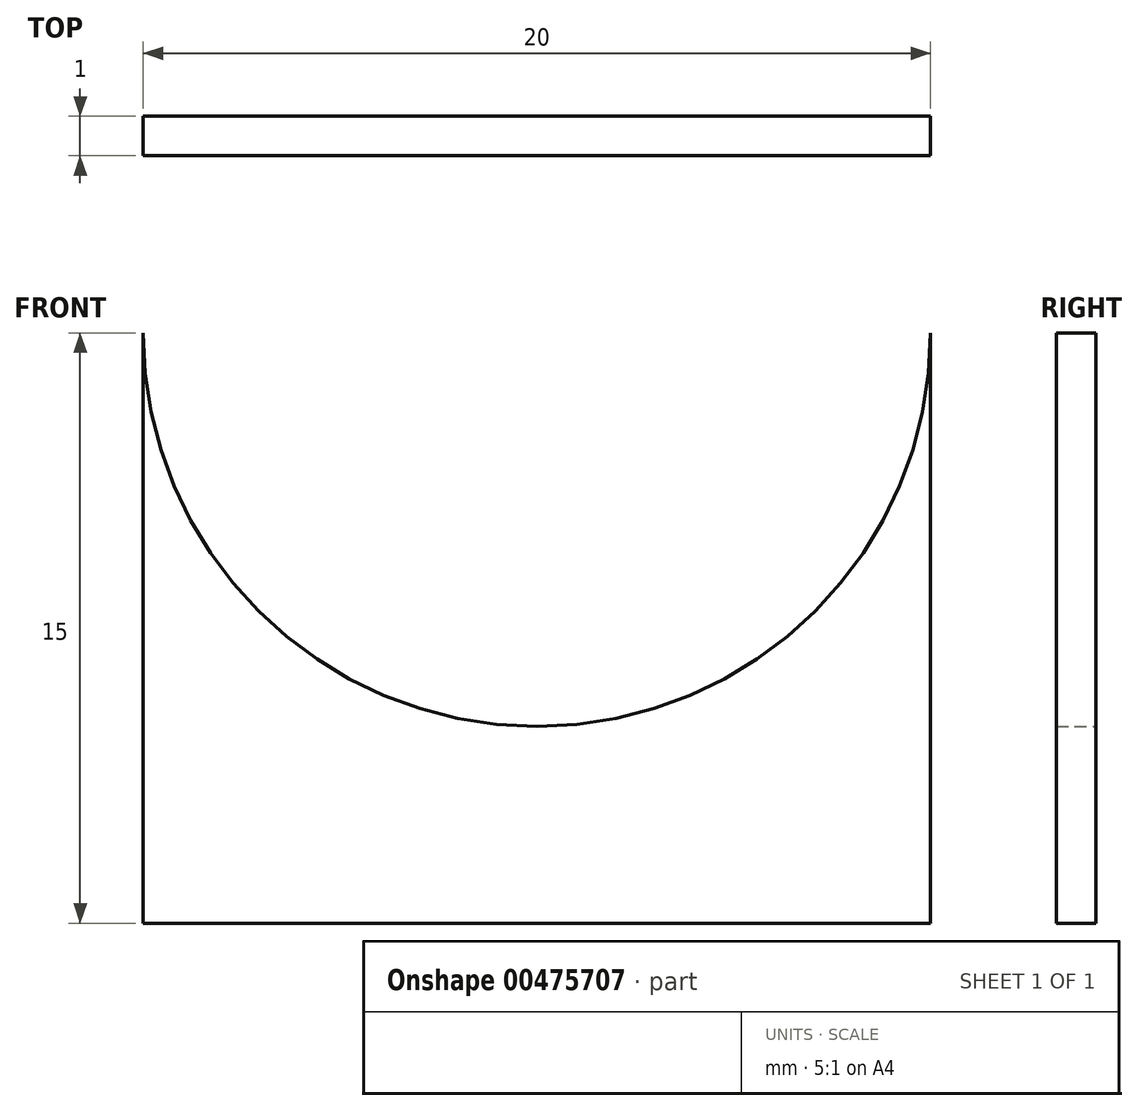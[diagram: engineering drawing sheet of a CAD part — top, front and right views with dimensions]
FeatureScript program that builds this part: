
annotation { "Feature Type Name" : "Feature", "Feature Type Description" : "" }
export const myFeature = defineFeature(function(context is Context, id is Id, definition is map)
    precondition{}
    {
        {
            var Q0;
            Q0=qCreatedBy(makeId("Front.planeOp"),FACE);
            var sketch = newSketch(context, id + "F0", { "sketchPlane" : qUnion([Q0])});
            skArc(sketch, "E0", {"start": v(-10, 0) * mm, "mid": v(0, -10) * mm, "end": v(10, 0) * mm});
            skLineSegment(sketch, "E1", {"start": v(-10, 0) * mm, "end": v(-10, -15) * mm});
            skLineSegment(sketch, "E2", {"start": v(10, 0) * mm, "end": v(10, -15) * mm});
            skLineSegment(sketch, "E3", {"start": v(-10, -15) * mm, "end": v(10, -15) * mm});
            skSolve(sketch);
        }
        {
            var Q0;
            Q0 = qSketchRegion(id + "F0", true);
            extrude(context, id + "F1", {"entities" : qUnion([Q0]), "depth" : 1 * mm, "offsetDistance" : 25 * mm});
        }
    });
